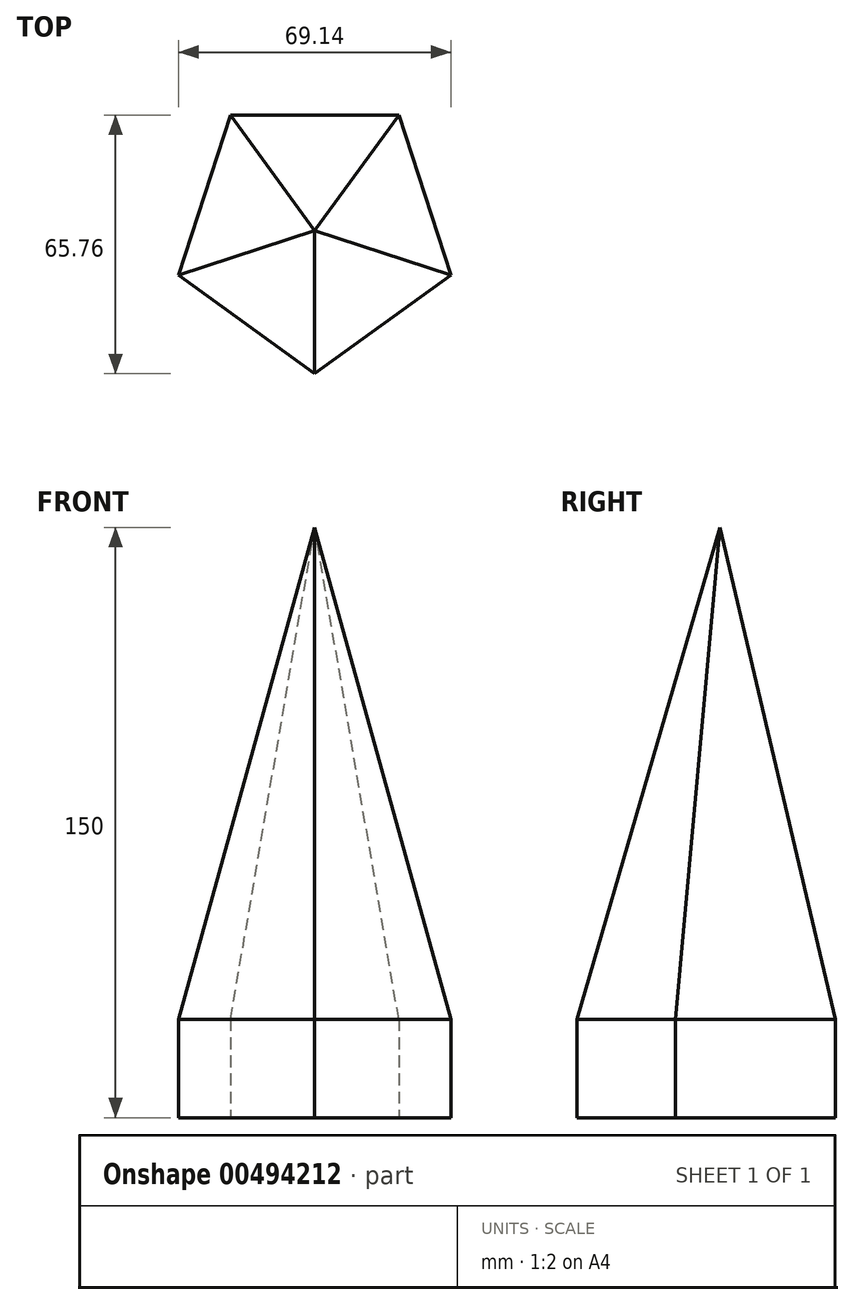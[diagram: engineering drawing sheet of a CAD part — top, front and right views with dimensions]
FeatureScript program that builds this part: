
annotation { "Feature Type Name" : "Feature", "Feature Type Description" : "" }
export const myFeature = defineFeature(function(context is Context, id is Id, definition is map)
    precondition{}
    {
        {
            var Q0;
            Q0=qCreatedBy(makeId("Top.planeOp"),FACE);
            var sketch = newSketch(context, id + "F0", { "sketchPlane" : qUnion([Q0])});
            skCircle(sketch, "E0.cCircle", {"center": v(0, 0) * mm, "radius": 29.4 * mm, "construction": true});
            skLineSegment(sketch, "E0.0", {"start": v(-21.36, 29.4) * mm, "end": v(21.36, 29.4) * mm});
            skLineSegment(sketch, "E0.1", {"start": v(21.36, 29.4) * mm, "end": v(34.57, -11.23) * mm});
            skLineSegment(sketch, "E0.2", {"start": v(34.57, -11.23) * mm, "end": v(0, -36.35) * mm});
            skLineSegment(sketch, "E0.3", {"start": v(0, -36.35) * mm, "end": v(-34.57, -11.23) * mm});
            skLineSegment(sketch, "E0.4", {"start": v(-34.57, -11.23) * mm, "end": v(-21.36, 29.4) * mm});
            skPoint(sketch, "E0.0.midPoint", {"position": v(0, 29.4) * mm});
            skSolve(sketch);
        }
        {
            var Q0;
            Q0=makeQuery(id+"F0.imprint","IMPRINT",FACE,{"disambiguationData":[TD([[makeQuery(id+"F0.imprint","IMPRINT",EDGE,{"derivedFrom":sQuery(id+"F0.wireOp",EDGE,"E0.0")}),-1.0]])]});
            extrude(context, id + "F1", {"entities" : qUnion([Q0]), "depth" : 25 * mm});
        }
        {
            var Q0;
            Q0=qCreatedBy(makeId("Top.planeOp"),FACE);
            cPlane(context, id + "F2", {"entities" : qUnion([Q0]), "cplaneType" : CPlaneType.OFFSET, "offset" : 150 * mm, "width" : 150 * mm, "height" : 150 * mm});
        }
        {
            var Q0;
            Q0=qCreatedBy(id+"F2.planeOp",FACE);
            var sketch = newSketch(context, id + "F3", { "sketchPlane" : qUnion([Q0])});
            skPoint(sketch, "E1", {"position": v(0, 0) * mm});
            skSolve(sketch);
        }
        {
            var Q1;
            Q1=makeQuery(id+"F1.opExtrude","CAP_FACE",FACE,{"disambiguationData":[OSD([sQuery(id+"F0.wireOp",EDGE,"E0.0"),sQuery(id+"F0.wireOp",EDGE,"E0.1"),sQuery(id+"F0.wireOp",EDGE,"E0.2"),sQuery(id+"F0.wireOp",EDGE,"E0.3"),sQuery(id+"F0.wireOp",EDGE,"E0.4")])],"isStart":false});
            var Q2;
            Q2=sQuery(id+"F3.wireOp",VERTEX,"E1");
            loft(context, id + "F4", {"operationType" : NewBodyOperationType.ADD, "sheetProfilesArray" : [{ "sheetProfileEntities" : qUnion([Q1]) }, { "sheetProfileEntities" : qUnion([Q2]) }]});
        }
    });
